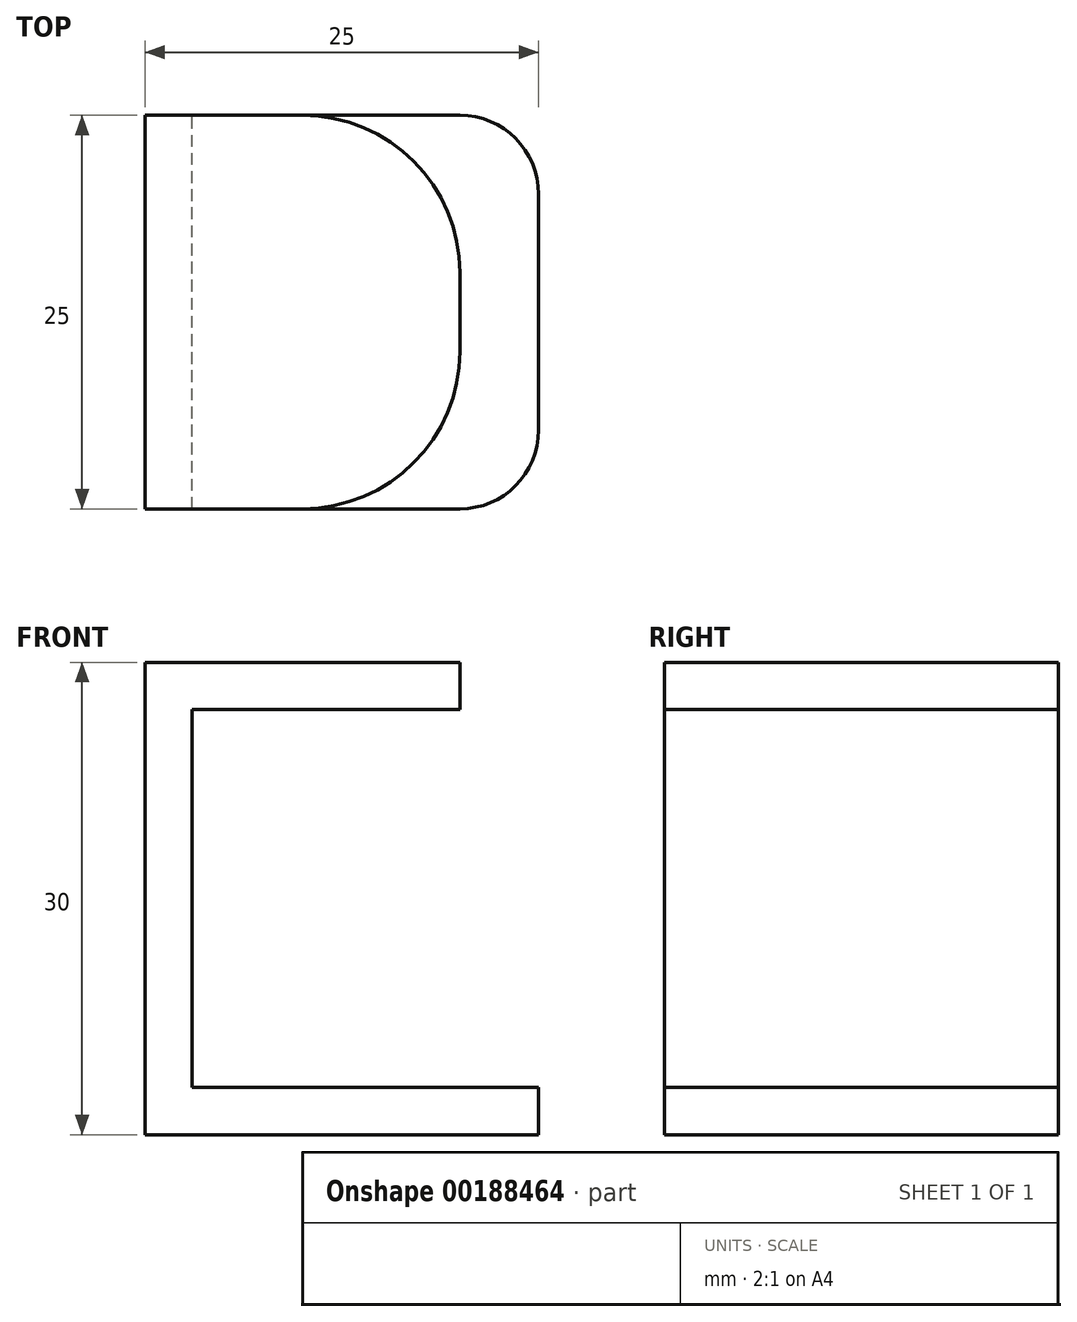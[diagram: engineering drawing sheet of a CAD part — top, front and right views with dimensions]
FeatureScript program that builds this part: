
annotation { "Feature Type Name" : "Feature", "Feature Type Description" : "" }
export const myFeature = defineFeature(function(context is Context, id is Id, definition is map)
    precondition{}
    {
        {
            var Q0;
            Q0=qCreatedBy(makeId("Front.planeOp"),FACE);
            var sketch = newSketch(context, id + "F0", { "sketchPlane" : qUnion([Q0])});
            skLineSegment(sketch, "E0.bottom", {"start": v(0, 0) * mm, "end": v(25, 0) * mm});
            skLineSegment(sketch, "E0.top", {"start": v(0, 3) * mm, "end": v(25, 3) * mm});
            skLineSegment(sketch, "E0.left", {"start": v(0, 0) * mm, "end": v(0, 3) * mm});
            skLineSegment(sketch, "E0.right", {"start": v(25, 0) * mm, "end": v(25, 3) * mm});
            skLineSegment(sketch, "E1.bottom", {"start": v(0, 0) * mm, "end": v(3, 0) * mm});
            skLineSegment(sketch, "E1.top", {"start": v(0, 30) * mm, "end": v(3, 30) * mm});
            skLineSegment(sketch, "E1.left", {"start": v(0, 0) * mm, "end": v(0, 30) * mm});
            skLineSegment(sketch, "E1.right", {"start": v(3, 0) * mm, "end": v(3, 30) * mm});
            skLineSegment(sketch, "E2.bottom", {"start": v(0, 30) * mm, "end": v(20, 30) * mm});
            skLineSegment(sketch, "E2.top", {"start": v(0, 27) * mm, "end": v(20, 27) * mm});
            skLineSegment(sketch, "E2.left", {"start": v(0, 30) * mm, "end": v(0, 27) * mm});
            skLineSegment(sketch, "E2.right", {"start": v(20, 30) * mm, "end": v(20, 27) * mm});
            skSolve(sketch);
        }
        {
            var Q0;
            Q0 = qSketchRegion(id + "F0", true);
            extrude(context, id + "F1", {"entities" : qUnion([Q0]), "endBound" : BoundingType.SYMMETRIC, "depth" : 25 * mm});
        }
        {
            var Q0;
            Q0=makeQuery(id+"F1.opExtrude","CAP_EDGE",EDGE,{"disambiguationData":[OSD([sQuery(id+"F0.wireOp",EDGE,"E2.right")])],"isStart":false});
            var Q1;
            Q1=makeQuery(id+"F1.opExtrude","CAP_EDGE",EDGE,{"disambiguationData":[OSD([sQuery(id+"F0.wireOp",EDGE,"E2.right")])],"isStart":true});
            fillet(context, id + "F2", {"entities" : qUnion([Q0, Q1]), "radius" : 10 * mm, "tangentPropagation" : true, "allowEdgeOverflow" : false});
        }
        {
            var Q0;
            Q0=makeQuery(id+"F1.opExtrude","CAP_EDGE",EDGE,{"disambiguationData":[OSD([sQuery(id+"F0.wireOp",EDGE,"E0.right")])],"isStart":false});
            var Q1;
            Q1=makeQuery(id+"F1.opExtrude","CAP_EDGE",EDGE,{"disambiguationData":[OSD([sQuery(id+"F0.wireOp",EDGE,"E0.right")])],"isStart":true});
            fillet(context, id + "F3", {"entities" : qUnion([Q0, Q1]), "radius" : 5 * mm, "tangentPropagation" : true, "allowEdgeOverflow" : false});
        }
    });
